# Revit family: CAME_Турникет_Скоростной_SLIDINGGATEGL_РаздвижнойБоковойМодуль
name_source: partatom
category: Специальное оборудование
units: mm (PartAtom-declared; Revit-internal decimal feet)

## family parameters
Всегда вертикально = Да
На основе рабочей плоскости = Нет
Общий = Нет
При загрузке вырезать с полостями = Нет
Размер круглого соединителя = Использовать диаметр
Тип детали = Нормальный
Точка расчета площади = Нет

## types (2) — shared parameters
ADSK_URL документации изделия = https://camerussia.com
ADSK_URL страницы изделия = https://camerussia.com
ADSK_Версия Revit = 2019
ADSK_Версия семейства = 1.0
ADSK_Группирование = SLIDING GATE
ADSK_Единица измерения = шт.
ADSK_Завод-изготовитель = CAME
ADSK_Классификация нагрузок = Прочее
ADSK_Код изделия = Код КСР 26.30.50.119.61.2.07.09
ADSK_Количество = 1
ADSK_Количество фаз = 1
ADSK_Коэффициент мощности = 0.96
ADSK_Напряжение = 230 В
ADSK_Номинальная мощность = 39 Вт
ADSK_Обозначение = ТУ 26.30.50-001-89603926-2021
ADSK_Полная мощность = 41 В·А
ADSK_Размер_Высота = 1010 мм
ADSK_Размер_Глубина = 1000 мм
BL_BIM library = https://bimlib.pro
CAME_Время открывания (с) = 0.5
CAME_Диапазон рабочих температур (°C) = -20 ÷ +68
CAME_Интенсивность использования (%) = ИНТЕНСИВНОЕ
CAME_Класс защиты (IP) = 44
CAME_Максимальное количество проходов в минуту = 30
CAME_Напряжение электропитания двигателя (В) = 24 В
CAME_Тип механизма турникета = моторизованный
URL = https://camerussia.com
Группа модели = Турникеты
Изготовитель = CAME

## per-type parameters (varying)
| type | 550 | 900 | ADSK_Марка | ADSK_Масса | ADSK_Масса_Текст | ADSK_Наименование | ADSK_Наименование краткое | ADSK_Размер_Ширина | Описание |
| 550 | Да | Нет | АРТ:001SGL02S | 59 | 59 | Боковой модуль раздвижного турникета SLIDING GATE GL, ширина прохода 550 мм, левый или правый | Бок. модуль турникета SLIDING GATE GL, 550 мм, левый или правый | 575 мм | Боковой модуль раздвижного турникета SLIDING GATE GL. Оснащен платой управления и светодиодными указателями прохода и направления. Корпус - нержавеющая сталь AISI 304. Сервопозиционный электропривод створки с определением препятствий и автоматической разблокировкой при отключении электроэнергии. Створка из 10 мм закаленного стекла. Ширина прохода 550 мм. Высота створки 900 мм. Время открытия - 0.5 сек. Встроенный блок питания. |
| 900 | Нет | Да | АРТ:001SGL90S | 68 | 68 | Боковой модуль раздвижного турникета SLIDING GATE GL90, ширина прохода 900 мм, левый или правый | Бок. модуль турникета SLIDING GATE GL90, 900 мм, левый или правый | 700 мм | Боковой модуль раздвижного турникета SLIDING GATE GL90. Оснащен платой управления и светодиодными указателями прохода и направления. Корпус - нержавеющая сталь AISI 304. Сервопозиционный электропривод створки с определением препятствий и автоматической разблокировкой при отключении электроэнергии. Створка из 10 мм закаленного стекла. Ширина прохода 900 мм. Высота створки 900 мм. Время открытия - 0.5 сек. Встроенный блок питания. |
